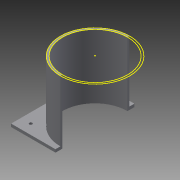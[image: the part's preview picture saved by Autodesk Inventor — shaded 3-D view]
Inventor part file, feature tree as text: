
AUTODESK INVENTOR PART (.ipt)
format: ipt  version: 2013 (Build 170138000, 138)  size: 120,320 bytes
history: native  units: mm
features: sketch x6, extrude x4, other x1, hole x1
ambient origin geometry x8: Origin, YZ Plane, XZ Plane, XY Plane, X Axis, Y Axis, Z Axis, Center Point
feature tree (12):
  other  "ソリッド1"
  extrude  "押し出し1"  Depth=70.0mm
  extrude  "押し出し2"  Depth=66.0mm
  extrude  "押し出し3"  Depth=90.0mm
  sketch  "スケッチ4"
  hole  "穴1"  [1 undecoded]
  extrude  "押し出し4"  Depth=3.0mm TaperAngle=0.0deg
  sketch  "スケッチ1"
  sketch  "スケッチ2"
  sketch  "スケッチ3"
  sketch  "スケッチ5"
  sketch  "スケッチ6"
note: 1 required parameter value undecoded (feature->parameter linkage not recoverable at this tier; creation-order binding heuristic only, values carry confidence <= 0.55)
